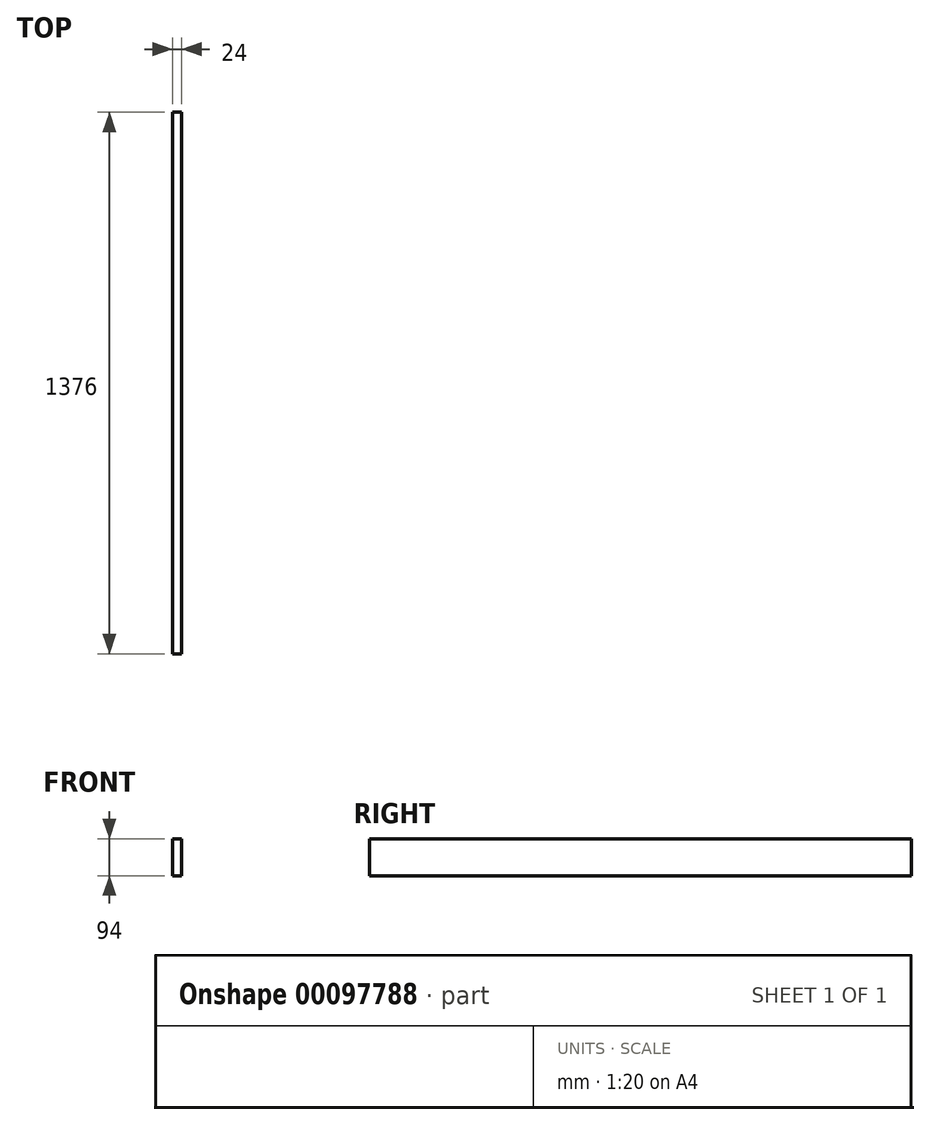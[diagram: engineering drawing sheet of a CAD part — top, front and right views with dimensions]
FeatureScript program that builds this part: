
annotation { "Feature Type Name" : "Feature", "Feature Type Description" : "" }
export const myFeature = defineFeature(function(context is Context, id is Id, definition is map)
    precondition{}
    {
        {
            var Q0;
            Q0=qCreatedBy(makeId("Front.planeOp"),FACE);
            var sketch = newSketch(context, id + "F0", { "sketchPlane" : qUnion([Q0])});
            skLineSegment(sketch, "E0.bottom", {"start": v(0, 0) * mm, "end": v(24, 0) * mm});
            skLineSegment(sketch, "E0.top", {"start": v(0, 94) * mm, "end": v(24, 94) * mm});
            skLineSegment(sketch, "E0.left", {"start": v(0, 0) * mm, "end": v(0, 94) * mm});
            skLineSegment(sketch, "E0.right", {"start": v(24, 0) * mm, "end": v(24, 94) * mm});
            skSolve(sketch);
        }
        {
            var Q0;
            Q0=qSketchRegion(id+"F0",true);
            extrude(context, id + "F1", {"entities" : qUnion([Q0]), "oppositeDirection" : true, "depth" : 1376 * mm});
        }
    });
